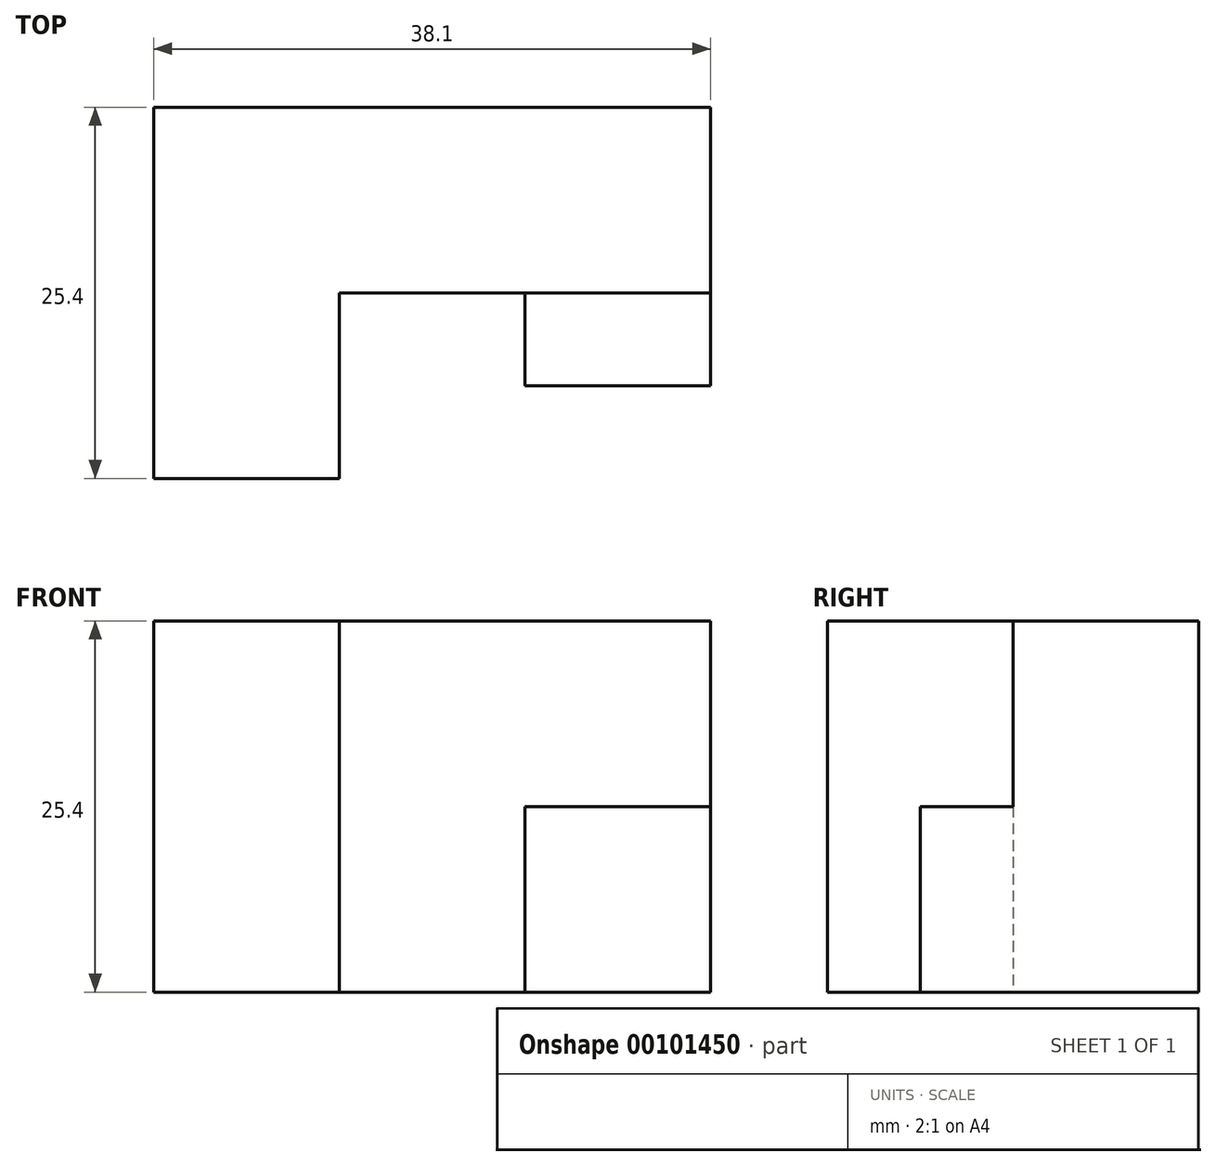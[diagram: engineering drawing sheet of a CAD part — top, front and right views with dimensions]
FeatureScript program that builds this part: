
annotation { "Feature Type Name" : "Feature", "Feature Type Description" : "" }
export const myFeature = defineFeature(function(context is Context, id is Id, definition is map)
    precondition{}
    {
        {
            var Q0;
            Q0=qCreatedBy(makeId("Top.planeOp"),FACE);
            var sketch = newSketch(context, id + "F0", { "sketchPlane" : qUnion([Q0])});
            skLineSegment(sketch, "E0", {"start": v(0, 0) * mm, "end": v(38.1, 0) * mm});
            skLineSegment(sketch, "E1", {"start": v(38.1, 0) * mm, "end": v(38.1, -12.7) * mm});
            skLineSegment(sketch, "E2", {"start": v(38.1, -12.7) * mm, "end": v(12.7, -12.7) * mm});
            skLineSegment(sketch, "E3", {"start": v(12.7, -12.7) * mm, "end": v(12.7, -25.4) * mm});
            skLineSegment(sketch, "E4", {"start": v(12.7, -25.4) * mm, "end": v(0, -25.4) * mm});
            skLineSegment(sketch, "E5", {"start": v(0, -25.4) * mm, "end": v(0, 0) * mm});
            skSolve(sketch);
        }
        {
            var Q0;
            Q0 = qSketchRegion(id + "F0", true);
            extrude(context, id + "F1", {"entities" : qUnion([Q0]), "depth" : 25.4 * mm});
        }
        {
            var Q0;
            Q0=makeQuery(id+"F1.opExtrude","SWEPT_FACE",FACE,{"disambiguationData":[OSD([sQuery(id+"F0.wireOp",EDGE,"E2")])]});
            var sketch = newSketch(context, id + "F2", { "sketchPlane" : qUnion([Q0])});
            skLineSegment(sketch, "E6", {"start": v(38.1, 0) * mm, "end": v(38.1, 12.7) * mm});
            skLineSegment(sketch, "E7", {"start": v(38.1, 12.7) * mm, "end": v(25.4, 12.7) * mm});
            skLineSegment(sketch, "E8", {"start": v(25.4, 12.7) * mm, "end": v(25.4, 0) * mm});
            skLineSegment(sketch, "E9", {"start": v(25.4, 0) * mm, "end": v(38.1, 0) * mm});
            skSolve(sketch);
        }
        {
            var Q0;
            Q0 = qSketchRegion(id + "F2", true);
            extrude(context, id + "F3", {"entities" : qUnion([Q0]), "operationType" : NewBodyOperationType.ADD, "depth" : 6.35 * mm});
        }
    });
